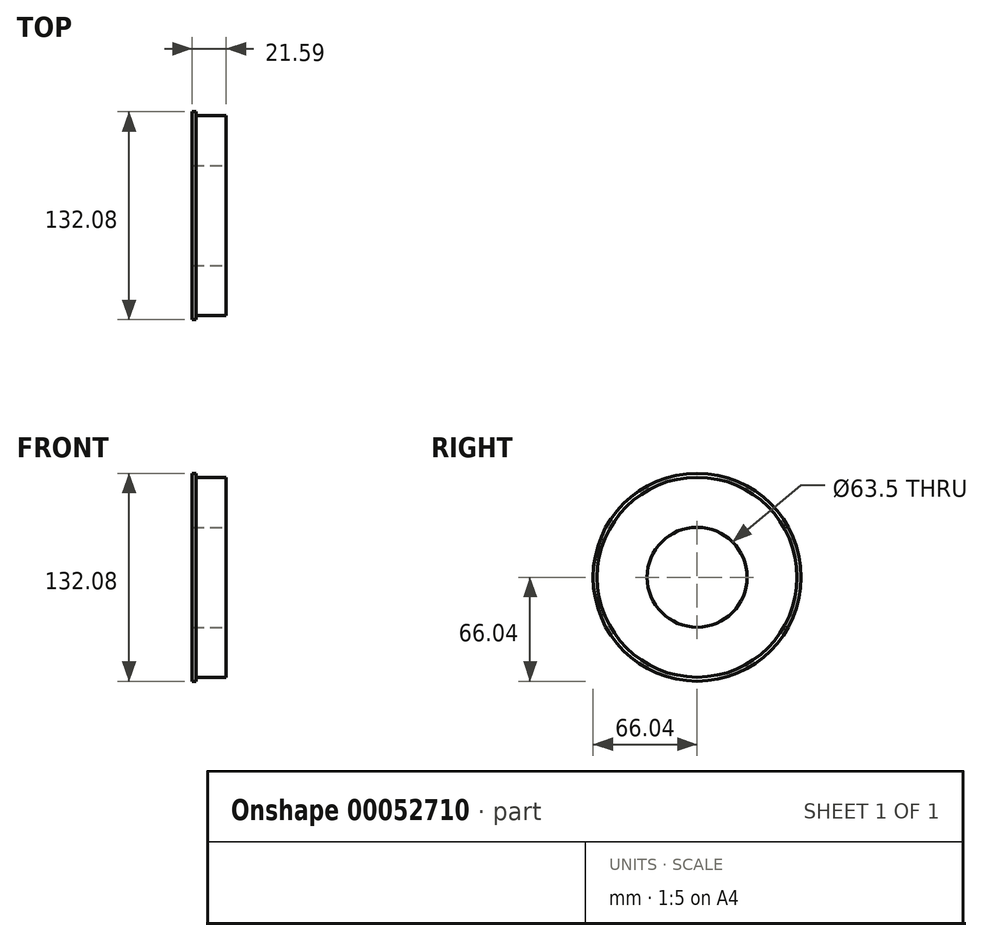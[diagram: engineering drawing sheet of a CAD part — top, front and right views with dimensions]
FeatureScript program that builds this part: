
annotation { "Feature Type Name" : "Feature", "Feature Type Description" : "" }
export const myFeature = defineFeature(function(context is Context, id is Id, definition is map)
    precondition{}
    {
        {
            var Q0;
            Q0=qCreatedBy(makeId("Right.planeOp"),FACE);
            var sketch = newSketch(context, id + "F0", { "sketchPlane" : qUnion([Q0])});
            skCircle(sketch, "E0", {"center": v(0, 0) * mm, "radius": 31.75 * mm});
            skCircle(sketch, "E1", {"center": v(0, 0) * mm, "radius": 63.5 * mm});
            skSolve(sketch);
        }
        {
            var Q0;
            Q0=makeQuery(id+"F0.imprint","IMPRINT",FACE,{"disambiguationData":[TD([[makeQuery(id+"F0.imprint","IMPRINT",EDGE,{"derivedFrom":sQuery(id+"F0.wireOp",EDGE,"E0")}),-1.0]])]});
            extrude(context, id + "F1", {"entities" : qUnion([Q0]), "oppositeDirection" : true, "depth" : 19.05 * mm});
        }
        {
            var Q0;
            Q0=makeQuery(id+"F1.opExtrude","CAP_FACE",FACE,{"disambiguationData":[OSD([sQuery(id+"F0.wireOp",EDGE,"E0"),sQuery(id+"F0.wireOp",EDGE,"E1")])],"isStart":false});
            var sketch = newSketch(context, id + "F2", { "sketchPlane" : qUnion([Q0])});
            skCircle(sketch, "E2.0", {"center": v(0, 0) * mm, "radius": 66.04 * mm});
            skCircle(sketch, "E3.0", {"center": v(0, 0) * mm, "radius": 31.75 * mm});
            skSolve(sketch);
        }
        {
            var Q0;
            Q0=makeQuery(id+"F2.imprint","IMPRINT",FACE,{"disambiguationData":[TD([[makeQuery(id+"F2.imprint","IMPRINT",EDGE,{"derivedFrom":sQuery(id+"F2.wireOp",EDGE,"E2.0")}),1.0]])]});
            var Q1;
            Q1=makeQuery(id+"F2.imprint","IMPRINT",FACE,{"disambiguationData":[TD([[makeQuery(id+"F2.imprint","IMPRINT",EDGE,{"derivedFrom":sQuery(id+"F2.wireOp",EDGE,"E3.0")}),1.0]])]});
            extrude(context, id + "F3", {"entities" : qUnion([Q0, Q1]), "operationType" : NewBodyOperationType.ADD, "depth" : 2.54 * mm});
        }
    });
